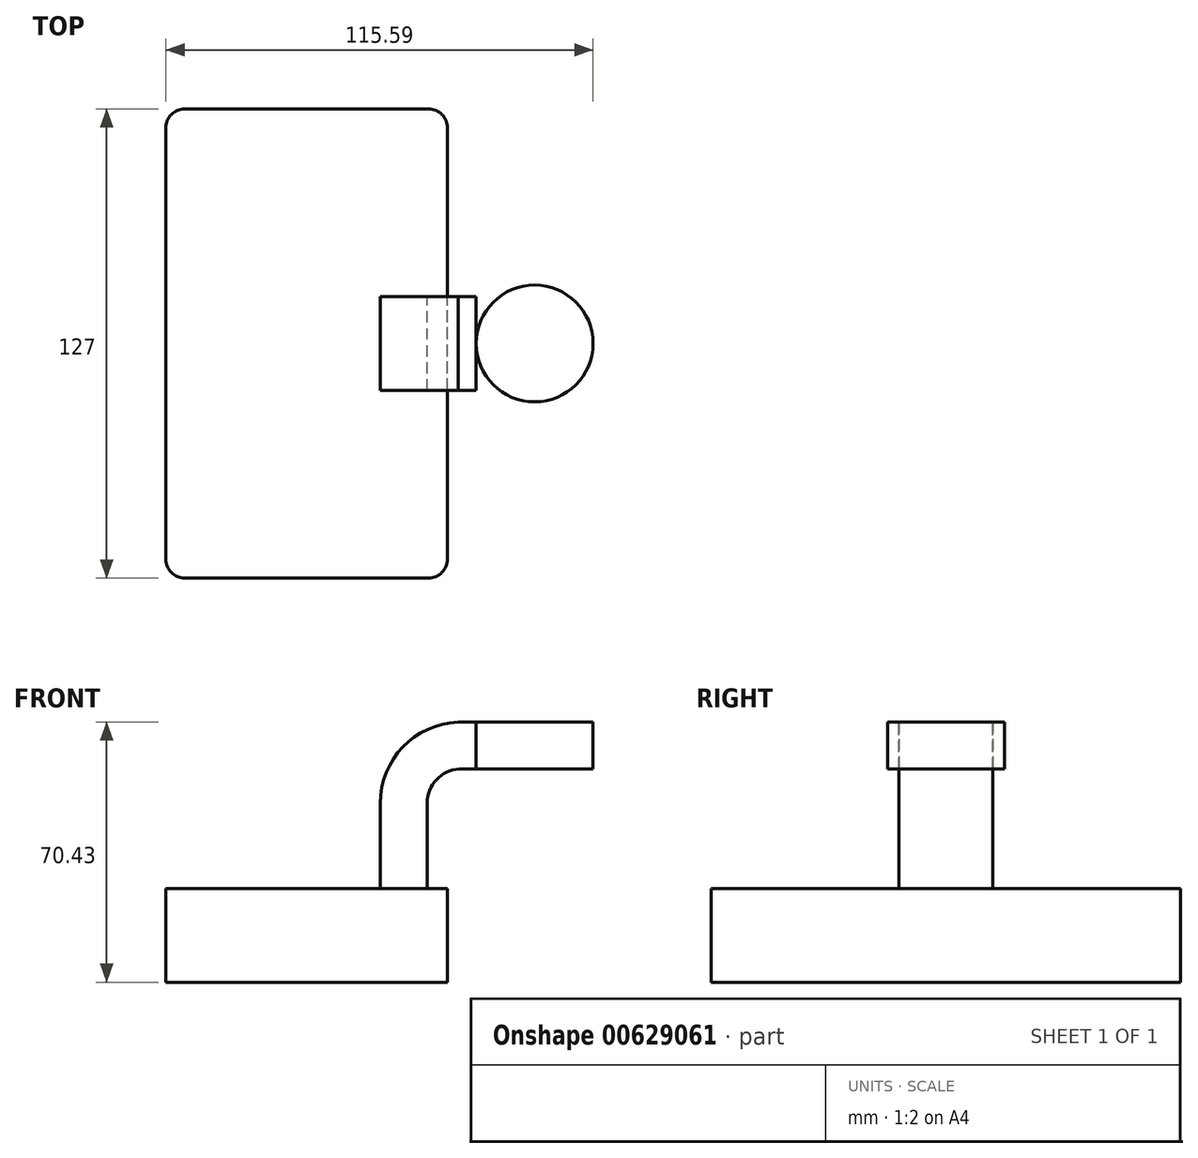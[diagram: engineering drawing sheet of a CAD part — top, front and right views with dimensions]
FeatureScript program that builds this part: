
annotation { "Feature Type Name" : "Feature", "Feature Type Description" : "" }
export const myFeature = defineFeature(function(context is Context, id is Id, definition is map)
    precondition{}
    {
        {
            var Q0;
            Q0=qCreatedBy(makeId("Front.planeOp"),FACE);
            var sketch = newSketch(context, id + "F0", { "sketchPlane" : qUnion([Q0])});
            skLineSegment(sketch, "E0.bottom", {"start": v(38.1, -12.7) * mm, "end": v(-38.1, -12.7) * mm});
            skLineSegment(sketch, "E0.top", {"start": v(38.1, 12.7) * mm, "end": v(-38.1, 12.7) * mm});
            skLineSegment(sketch, "E0.left", {"start": v(38.1, -12.7) * mm, "end": v(38.1, 12.7) * mm});
            skLineSegment(sketch, "E0.right", {"start": v(-38.1, -12.7) * mm, "end": v(-38.1, 12.7) * mm});
            skPoint(sketch, "E0.middle", {"position": v(0, 0) * mm});
            skLineSegment(sketch, "E1.bottom", {"start": v(77.5, 42.41) * mm, "end": v(45.86, 42.41) * mm});
            skLineSegment(sketch, "E1.top", {"start": v(77.5, 58.52) * mm, "end": v(45.86, 58.52) * mm});
            skLineSegment(sketch, "E1.left", {"start": v(77.5, 42.41) * mm, "end": v(77.5, 58.52) * mm});
            skLineSegment(sketch, "E1.right", {"start": v(45.86, 42.41) * mm, "end": v(45.86, 58.52) * mm});
            skPoint(sketch, "E1.middle", {"position": v(61.68, 50.46) * mm});
            skLineSegment(sketch, "E2", {"start": v(32.62, 12.7) * mm, "end": v(32.62, 35.78) * mm});
            skPoint(sketch, "E3", {"position": v(32.62, 35.78) * mm});
            skPoint(sketch, "E4", {"position": v(41.28, 45.03) * mm});
            skArc(sketch, "E5", {"start": v(41.28, 45.03) * mm, "mid": v(35.12, 42.1) * mm, "end": v(32.62, 35.78) * mm});
            skLineSegment(sketch, "E6", {"start": v(41.28, 45.03) * mm, "end": v(61.68, 45.03) * mm});
            skPoint(sketch, "E6.endSnap0", {"position": v(61.68, 42.41) * mm});
            skLineSegment(sketch, "E7", {"start": v(61.68, 45.03) * mm, "end": v(41.28, 45.03) * mm});
            skLineSegment(sketch, "E8.0", {"start": v(19.92, 12.7) * mm, "end": v(19.92, 35.78) * mm});
            skArc(sketch, "E8.1", {"start": v(40.94, 57.73) * mm, "mid": v(26.02, 50.97) * mm, "end": v(19.92, 35.78) * mm});
            skLineSegment(sketch, "E8.2", {"start": v(61.68, 57.73) * mm, "end": v(40.94, 57.73) * mm});
            skLineSegment(sketch, "E9", {"start": v(61.68, 57.73) * mm, "end": v(61.68, 45.03) * mm});
            skLineSegment(sketch, "E10", {"start": v(19.92, 12.7) * mm, "end": v(32.62, 12.7) * mm});
            skSolve(sketch);
        }
        {
            var Q0;
            Q0=makeQuery(id+"F0.imprint","IMPRINT",FACE,{"disambiguationData":[TD([[makeQuery(id+"F0.imprint","IMPRINT",EDGE,{"derivedFrom":sQuery(id+"F0.wireOp",EDGE,"E0.bottom")}),-1.0]])]});
            extrude(context, id + "F1", {"entities" : qUnion([Q0]), "endBound" : BoundingType.SYMMETRIC, "depth" : 127 * mm, "offsetDistance" : 25.4 * mm});
        }
        {
            var Q0;
            Q0=makeQuery(id+"F0.imprint","IMPRINT",FACE,{"disambiguationData":[TD([[makeQuery(id+"F0.imprint","IMPRINT",EDGE,{"derivedFrom":sQuery(id+"F0.wireOp",EDGE,"E2")}),1.0]])]});
            extrude(context, id + "F2", {"entities" : qUnion([Q0]), "operationType" : NewBodyOperationType.ADD, "endBound" : BoundingType.SYMMETRIC, "depth" : 25.4 * mm, "offsetDistance" : 25.4 * mm});
        }
        {
            var Q0;
            {var subQ5=sQuery(id+"F0.wireOp",EDGE,"E9");Q0=makeQuery(id+"F0.imprint","IMPRINT",FACE,{"disambiguationData":[TD([[makeQuery(id+"F0.imprint","IMPRINT",EDGE,{"derivedFrom":subQ5}),-1.0]])]});}
            var Q1;
            Q1=sQuery(id+"F0.wireOp",EDGE,"E9");
            var Q2;
            Q2=sQuery(id+"F0.wireOp",EDGE,"E9");
            revolve(context, id + "F3", {"entities" : qUnion([Q0]), "surfaceEntities" : qUnion([Q1]), "axis" : qUnion([Q2]), "revolveType" : RevolveType.SYMMETRIC, "angle" : 360 * degree});
        }
        {
            var Q0;
            Q0=makeQuery(id+"F1.opExtrude","CAP_EDGE",EDGE,{"disambiguationData":[OSD([sQuery(id+"F0.wireOp",EDGE,"E0.right")])],"isStart":false});
            var Q1;
            Q1=makeQuery(id+"F1.opExtrude","CAP_EDGE",EDGE,{"disambiguationData":[OSD([sQuery(id+"F0.wireOp",EDGE,"E0.left")])],"isStart":false});
            var Q2;
            Q2=makeQuery(id+"F1.opExtrude","CAP_EDGE",EDGE,{"disambiguationData":[OSD([sQuery(id+"F0.wireOp",EDGE,"E0.right")])],"isStart":true});
            var Q3;
            Q3=makeQuery(id+"F1.opExtrude","CAP_EDGE",EDGE,{"disambiguationData":[OSD([sQuery(id+"F0.wireOp",EDGE,"E0.left")])],"isStart":true});
            fillet(context, id + "F4", {"entities" : qUnion([Q0, Q1, Q2, Q3]), "radius" : 5.08 * mm, "tangentPropagation" : true, "allowEdgeOverflow" : false});
        }
    });
